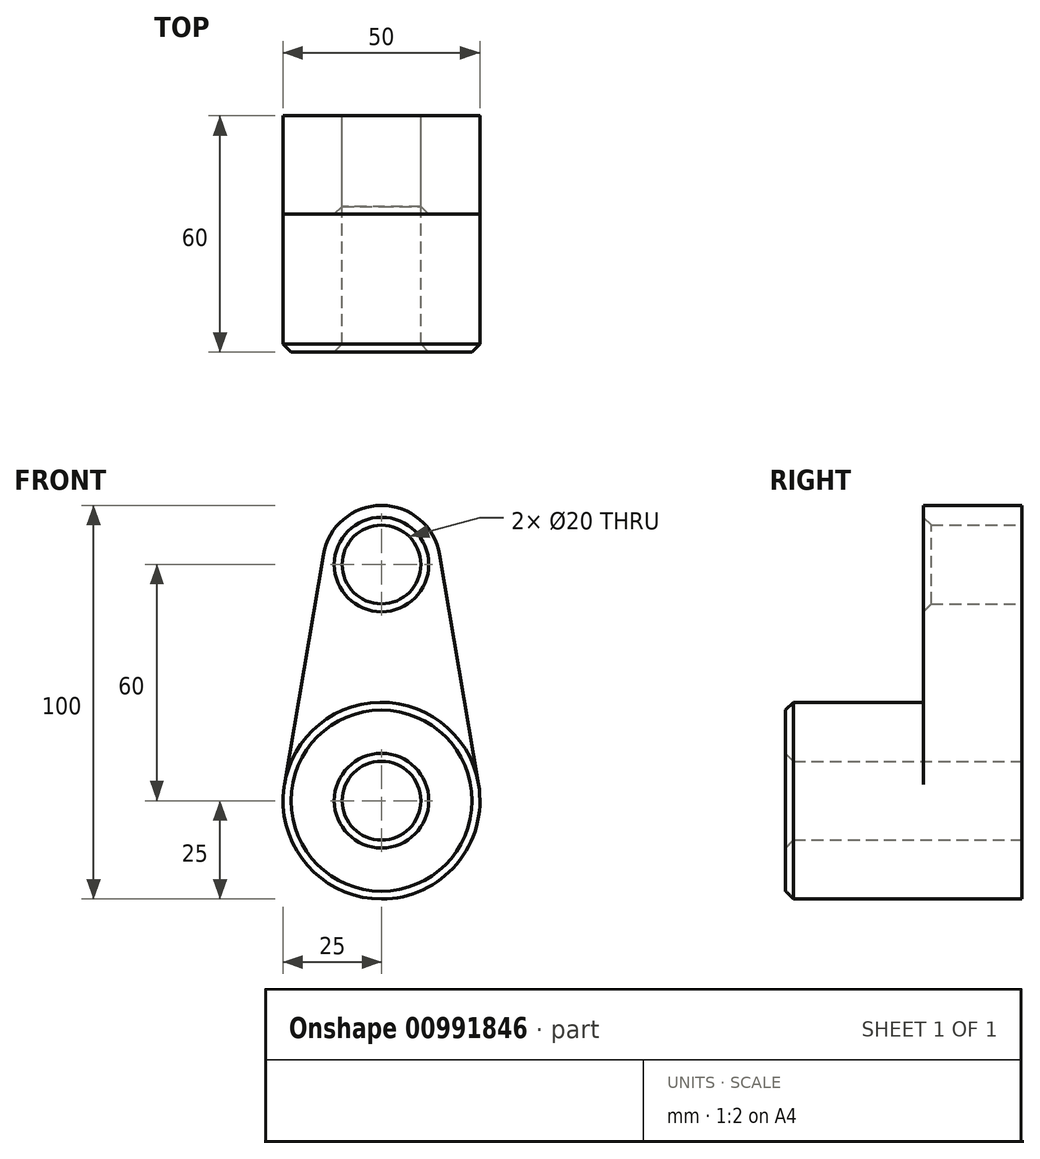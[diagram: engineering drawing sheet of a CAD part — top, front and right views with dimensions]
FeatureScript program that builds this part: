
annotation { "Feature Type Name" : "Feature", "Feature Type Description" : "" }
export const myFeature = defineFeature(function(context is Context, id is Id, definition is map)
    precondition{}
    {
        {
            var Q0;
            Q0=qCreatedBy(makeId("Front.planeOp"),FACE);
            var sketch = newSketch(context, id + "F0", { "sketchPlane" : qUnion([Q0])});
            skCircle(sketch, "E0", {"center": v(0, 0) * mm, "radius": 10 * mm});
            skCircle(sketch, "E1", {"center": v(0, 60) * mm, "radius": 10 * mm});
            skCircle(sketch, "E2", {"center": v(0, 60) * mm, "radius": 15 * mm});
            skCircle(sketch, "E3", {"center": v(0, 0) * mm, "radius": 25 * mm});
            skLineSegment(sketch, "E4", {"start": v(24.65, 4.17) * mm, "end": v(14.8, 62.5) * mm});
            skLineSegment(sketch, "E5", {"start": v(-24.65, 4.17) * mm, "end": v(-14.8, 62.5) * mm});
            skSolve(sketch);
        }
        {
            var Q0;
            Q0 = qSketchRegion(id + "F0", true);
            extrude(context, id + "F1", {"entities" : qUnion([Q0]), "depth" : 25 * mm, "offsetDistance" : 25 * mm});
        }
        {
            var Q0;
            Q0=makeQuery(id+"F0.imprint","IMPRINT",FACE,{"disambiguationData":[TD([[makeQuery(id+"F0.imprint","IMPRINT",EDGE,{"derivedFrom":sQuery(id+"F0.wireOp",EDGE,"E0")}),-1.0]])]});
            extrude(context, id + "F2", {"entities" : qUnion([Q0]), "operationType" : NewBodyOperationType.ADD, "depth" : 60 * mm, "offsetDistance" : 25 * mm});
        }
        {
            var Q0;
            Q0=makeQuery(id+"F2.opExtrude","CAP_EDGE",EDGE,{"disambiguationData":[OSD([sQuery(id+"F0.wireOp",EDGE,"E3")])],"isStart":false});
            var Q1;
            Q1=makeQuery(id+"F2.opExtrude","CAP_EDGE",EDGE,{"disambiguationData":[OSD([sQuery(id+"F0.wireOp",EDGE,"E0")])],"isStart":false});
            var Q2;
            Q2=makeQuery(id+"F1.opExtrude","CAP_EDGE",EDGE,{"disambiguationData":[OSD([sQuery(id+"F0.wireOp",EDGE,"E1")])],"isStart":false});
            chamfer(context, id + "F3", {"entities" : qUnion([Q0, Q1, Q2]), "width" : 2 * mm, "tangentPropagation" : true});
        }
    });
